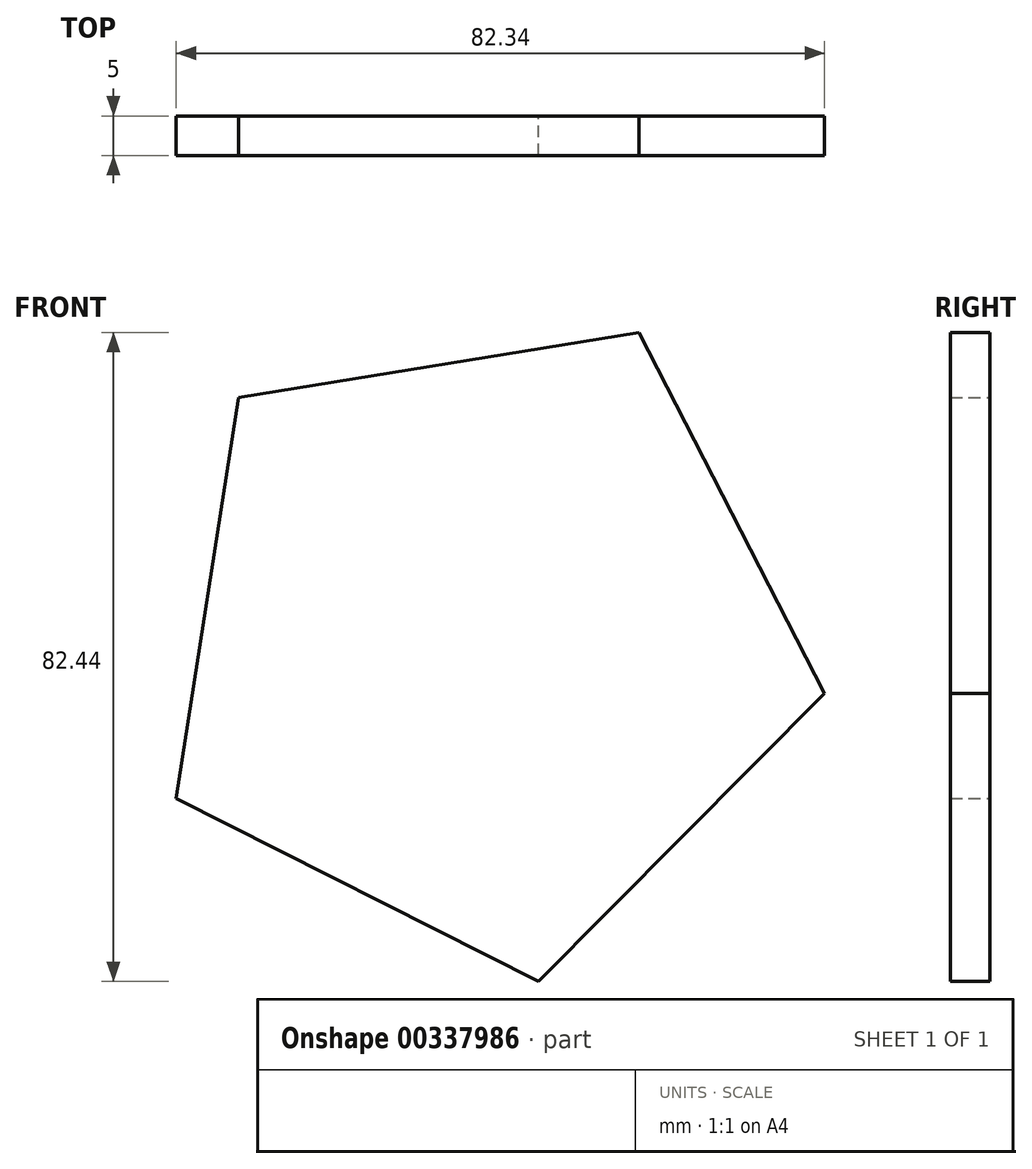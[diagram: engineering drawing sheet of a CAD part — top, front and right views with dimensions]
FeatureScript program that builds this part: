
annotation { "Feature Type Name" : "Feature", "Feature Type Description" : "" }
export const myFeature = defineFeature(function(context is Context, id is Id, definition is map)
    precondition{}
    {
        {
            var Q0;
            Q0=qCreatedBy(makeId("Front.planeOp"),FACE);
            var sketch = newSketch(context, id + "F0", { "sketchPlane" : qUnion([Q0])});
            skCircle(sketch, "E0.cCircle", {"center": v(-25.18, 25) * mm, "radius": 35.48 * mm, "construction": true});
            skLineSegment(sketch, "E0.0", {"start": v(18.16, 18.3) * mm, "end": v(-18.16, -18.3) * mm});
            skLineSegment(sketch, "E0.1", {"start": v(-18.16, -18.3) * mm, "end": v(-64.18, 4.94) * mm});
            skLineSegment(sketch, "E0.2", {"start": v(-64.18, 4.94) * mm, "end": v(-56.3, 55.89) * mm});
            skLineSegment(sketch, "E0.3", {"start": v(-56.3, 55.89) * mm, "end": v(-5.42, 64.14) * mm});
            skLineSegment(sketch, "E0.4", {"start": v(-5.42, 64.14) * mm, "end": v(18.16, 18.3) * mm});
            skPoint(sketch, "E0.0.midPoint", {"position": v(0, 0) * mm});
            skSolve(sketch);
        }
        {
            var Q0;
            Q0=makeQuery(id+"F0.imprint","IMPRINT",FACE,{"disambiguationData":[TD([[makeQuery(id+"F0.imprint","IMPRINT",EDGE,{"derivedFrom":sQuery(id+"F0.wireOp",EDGE,"E0.0")}),-1.0]])]});
            extrude(context, id + "F1", {"entities" : qUnion([Q0]), "depth" : 5 * mm});
        }
    });
